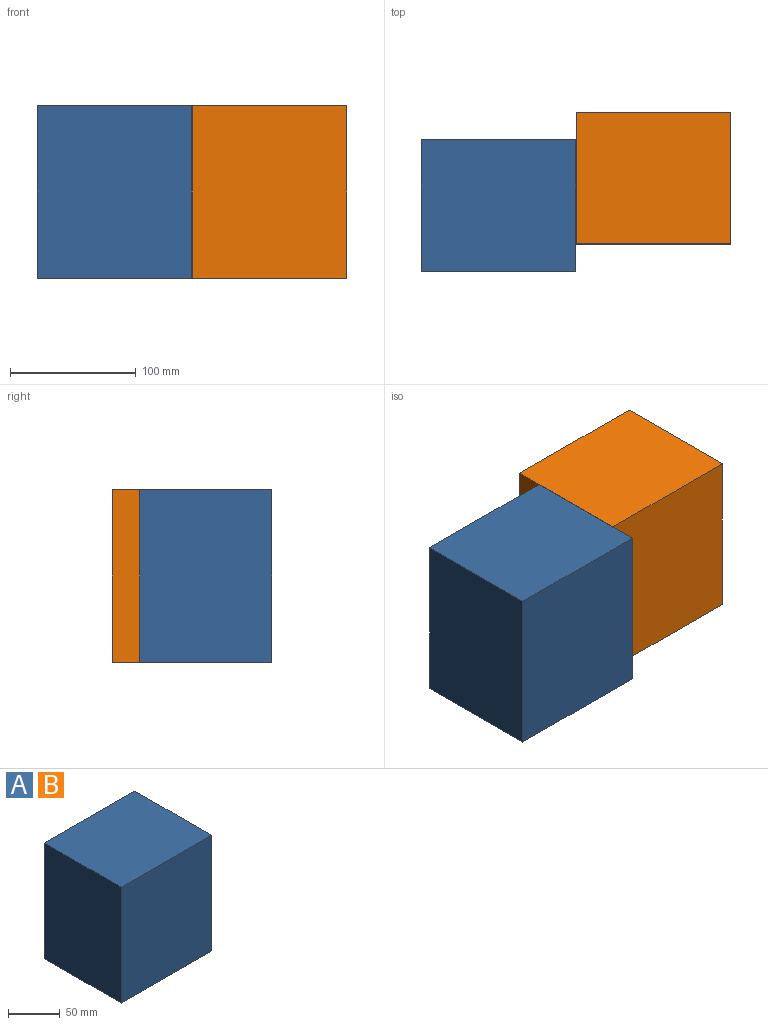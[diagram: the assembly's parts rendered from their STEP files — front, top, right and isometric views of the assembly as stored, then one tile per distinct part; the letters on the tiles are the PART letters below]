
ASSEMBLY  parts=2 mates=1
PART A: 6 faces, bbox 123.1x104.7x136.9 mm
  f0: plane 136.91x123.09mm, normal (0,-1,0), area 16852.2mm2, adj f1,f3,f4,f5
  f1: plane 136.91x104.7mm, normal (1,0,0), area 14333.9mm2, adj f0,f2,f4,f5
  f2: plane 136.91x123.09mm, normal (0,1,0), area 16852.2mm2, adj f1,f3,f4,f5
  f3: plane 136.91x104.7mm, normal (-1,0,0), area 14333.9mm2, adj f0,f2,f4,f5
  f4: plane 123.09x104.7mm, normal (0,0,1), area 12887.7mm2, adj f0,f1,f2,f3
  f5: plane 123.09x104.7mm, normal (0,0,-1), area 12887.7mm2, adj f0,f1,f2,f3
PART B: same geometry as A
PLACE A t=(-61.29,34.61,-37.25)mm
PLACE B t=(61.8,56.48,-37.25)mm
MATE fastened A.f4 <-> B.f4  axis (0,0,1) through (0.25,34.61,99.66)mm
